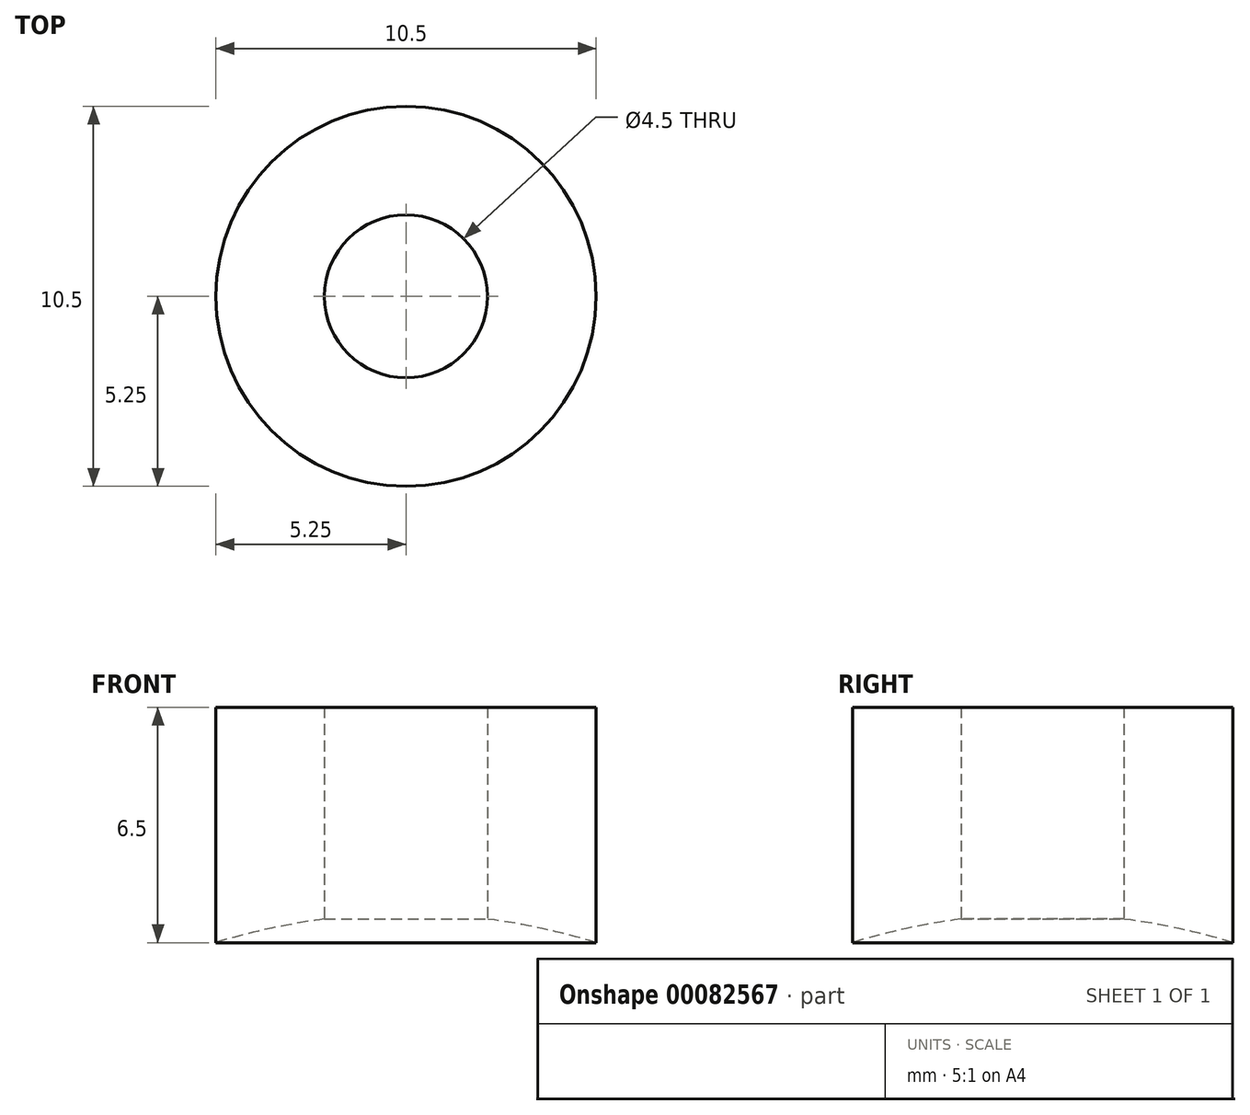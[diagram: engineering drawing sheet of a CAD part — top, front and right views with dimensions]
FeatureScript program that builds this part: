
annotation { "Feature Type Name" : "Feature", "Feature Type Description" : "" }
export const myFeature = defineFeature(function(context is Context, id is Id, definition is map)
    precondition{}
    {
        {
            var Q0;
            Q0=qCreatedBy(makeId("Front.planeOp"),FACE);
            var sketch = newSketch(context, id + "F0", { "sketchPlane" : qUnion([Q0])});
            skLineSegment(sketch, "E0", {"start": v(0, 0) * mm, "end": v(0, 5.08) * mm, "construction": true});
            skLineSegment(sketch, "E1", {"start": v(-2.25, 0) * mm, "end": v(-2.25, 5.85) * mm});
            skLineSegment(sketch, "E2", {"start": v(-2.25, 5.85) * mm, "end": v(-5.25, 5.85) * mm});
            skLineSegment(sketch, "E3", {"start": v(-5.25, 5.85) * mm, "end": v(-5.25, -0.65) * mm});
            skArc(sketch, "E4", {"start": v(-2.25, 0) * mm, "mid": v(-3.76, -0.26) * mm, "end": v(-5.25, -0.65) * mm});
            skSolve(sketch);
        }
        {
            var Q0;
            Q0 = qSketchRegion(id + "F0", true);
            var Q1;
            Q1=sQuery(id+"F0.wireOp",EDGE,"E0");
            revolve(context, id + "F1", {"entities" : qUnion([Q0]), "axis" : qUnion([Q1]), "revolveType" : RevolveType.FULL});
        }
    });
